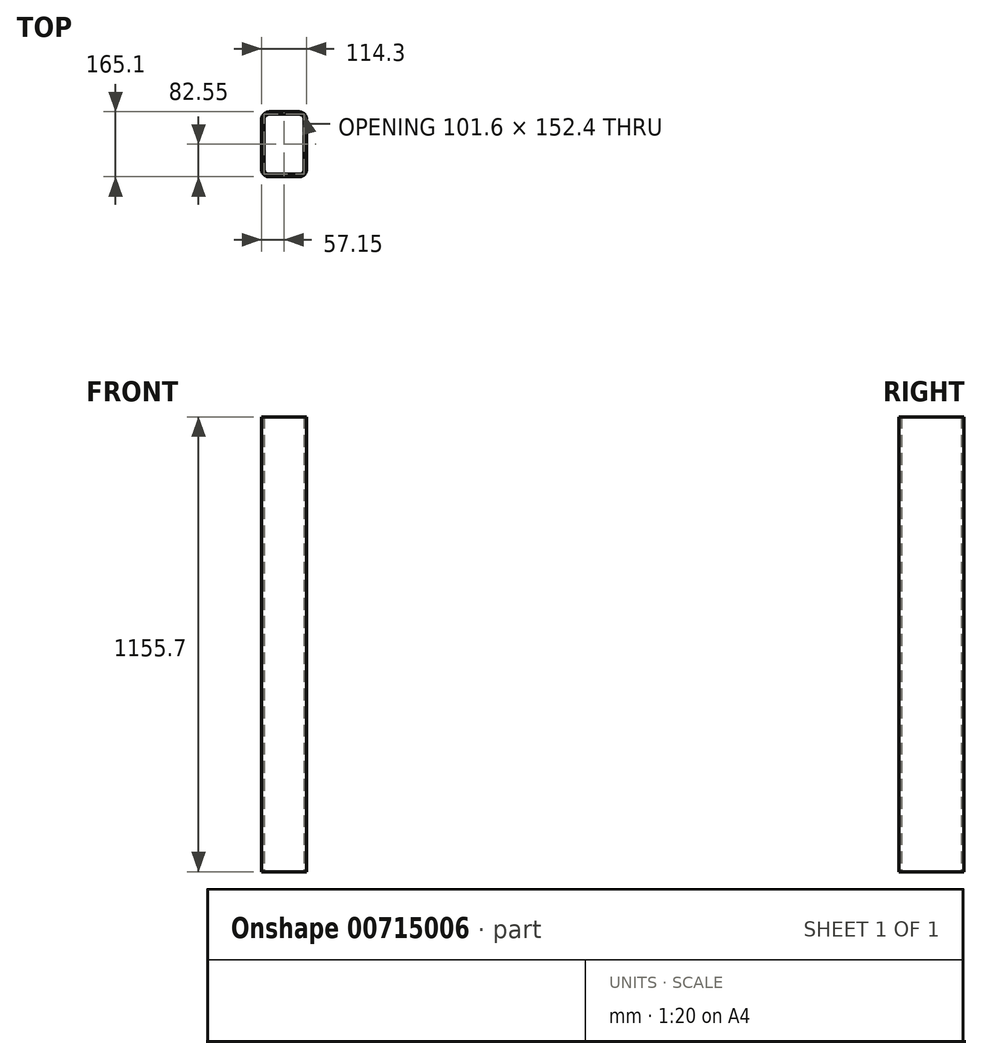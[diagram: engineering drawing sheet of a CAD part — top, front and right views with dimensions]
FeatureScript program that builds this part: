
annotation { "Feature Type Name" : "Feature", "Feature Type Description" : "" }
export const myFeature = defineFeature(function(context is Context, id is Id, definition is map)
    precondition{}
    {
        {
            var Q0;
            Q0=qCreatedBy(makeId("Top.planeOp"),FACE);
            var sketch = newSketch(context, id + "F0", { "sketchPlane" : qUnion([Q0])});
            skLineSegment(sketch, "E0.bottom", {"start": v(38.1, -76.2) * mm, "end": v(-38.1, -76.2) * mm});
            skLineSegment(sketch, "E0.top", {"start": v(38.1, 76.2) * mm, "end": v(-38.1, 76.2) * mm});
            skLineSegment(sketch, "E0.left", {"start": v(50.8, -63.5) * mm, "end": v(50.8, 63.5) * mm});
            skLineSegment(sketch, "E0.right", {"start": v(-50.8, -63.5) * mm, "end": v(-50.8, 63.5) * mm});
            skPoint(sketch, "E0.middle", {"position": v(0, 0) * mm});
            skPoint(sketch, "E1.visualSharp", {"position": v(-50.8, 76.2) * mm});
            skArc(sketch, "E1.filletArc", {"start": v(-38.1, 76.2) * mm, "mid": v(-47.08, 72.48) * mm, "end": v(-50.8, 63.5) * mm});
            skPoint(sketch, "E2.visualSharp", {"position": v(50.8, 76.2) * mm});
            skArc(sketch, "E2.filletArc", {"start": v(50.8, 63.5) * mm, "mid": v(47.08, 72.48) * mm, "end": v(38.1, 76.2) * mm});
            skPoint(sketch, "E3.visualSharp", {"position": v(50.8, -76.2) * mm});
            skArc(sketch, "E3.filletArc", {"start": v(38.1, -76.2) * mm, "mid": v(47.08, -72.48) * mm, "end": v(50.8, -63.5) * mm});
            skPoint(sketch, "E4.visualSharp", {"position": v(-50.8, -76.2) * mm});
            skArc(sketch, "E4.filletArc", {"start": v(-50.8, -63.5) * mm, "mid": v(-47.08, -72.48) * mm, "end": v(-38.1, -76.2) * mm});
            skLineSegment(sketch, "E5.0", {"start": v(57.15, -63.5) * mm, "end": v(57.15, 63.5) * mm});
            skArc(sketch, "E5.1", {"start": v(38.1, -82.55) * mm, "mid": v(51.57, -76.97) * mm, "end": v(57.15, -63.5) * mm});
            skArc(sketch, "E5.2", {"start": v(57.15, 63.5) * mm, "mid": v(51.57, 76.97) * mm, "end": v(38.1, 82.55) * mm});
            skLineSegment(sketch, "E5.3", {"start": v(38.1, -82.55) * mm, "end": v(-38.1, -82.55) * mm});
            skLineSegment(sketch, "E5.4", {"start": v(38.1, 82.55) * mm, "end": v(-38.1, 82.55) * mm});
            skArc(sketch, "E5.5", {"start": v(-38.1, 82.55) * mm, "mid": v(-51.57, 76.97) * mm, "end": v(-57.15, 63.5) * mm});
            skLineSegment(sketch, "E5.6", {"start": v(-57.15, -63.5) * mm, "end": v(-57.15, 63.5) * mm});
            skArc(sketch, "E5.7", {"start": v(-57.15, -63.5) * mm, "mid": v(-51.57, -76.97) * mm, "end": v(-38.1, -82.55) * mm});
            skSolve(sketch);
        }
        {
            var Q0;
            Q0=makeQuery(id+"F0.imprint","IMPRINT",FACE,{"disambiguationData":[TD([[makeQuery(id+"F0.imprint","IMPRINT",EDGE,{"derivedFrom":sQuery(id+"F0.wireOp",EDGE,"E0.bottom")}),1.0]])]});
            extrude(context, id + "F1", {"entities" : qUnion([Q0]), "depth" : 1155.7 * mm, "offsetDistance" : 25.4 * mm});
        }
    });
